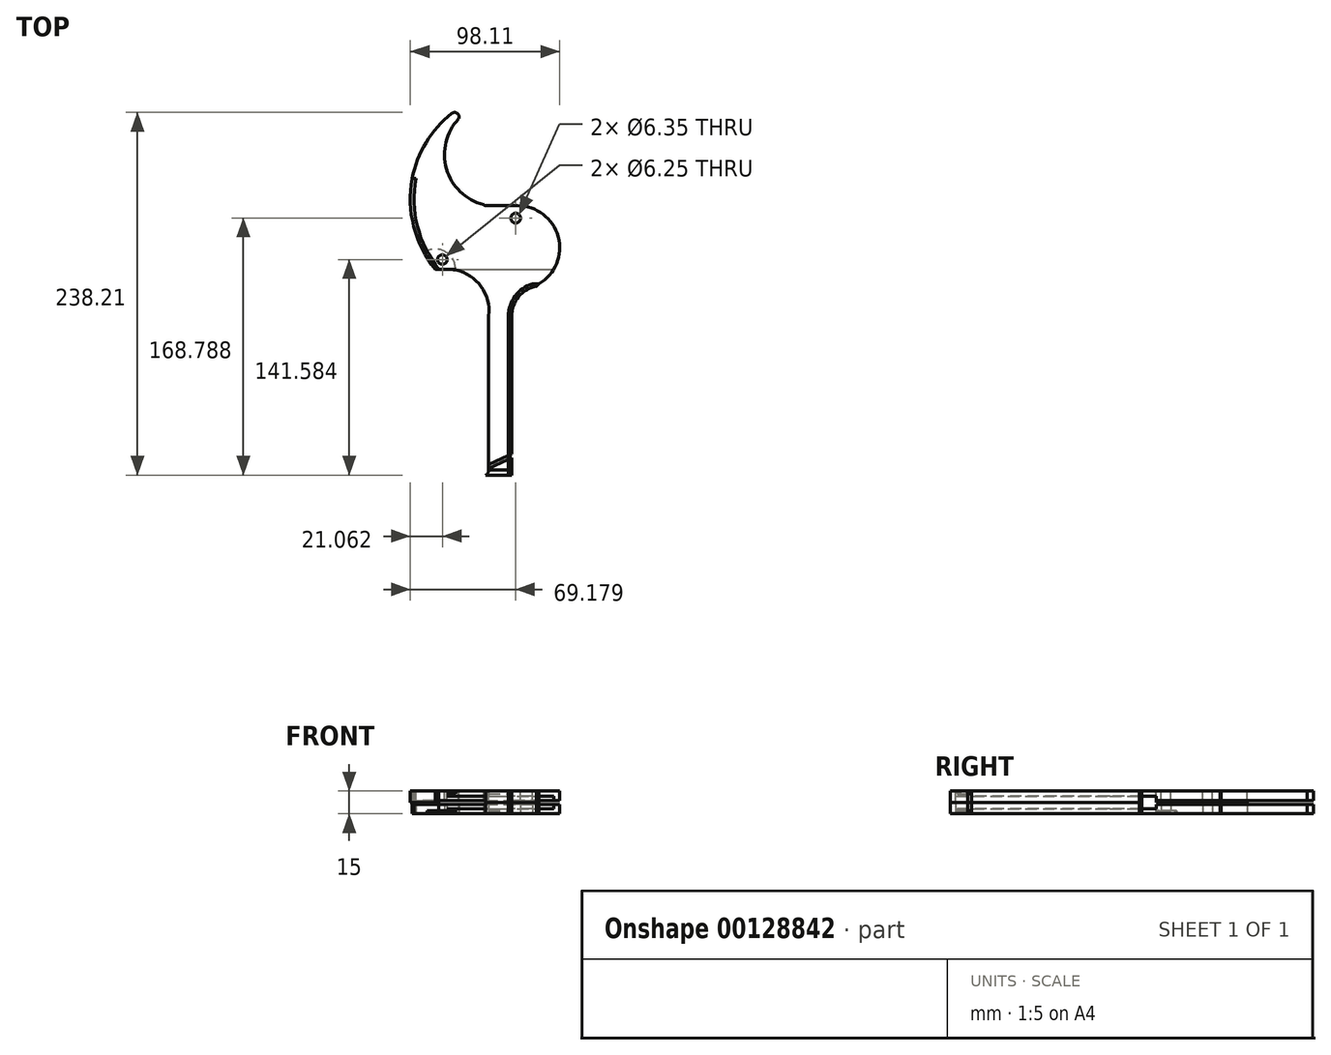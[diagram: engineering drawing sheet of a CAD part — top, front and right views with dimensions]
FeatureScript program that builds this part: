
annotation { "Feature Type Name" : "Feature", "Feature Type Description" : "" }
export const myFeature = defineFeature(function(context is Context, id is Id, definition is map)
    precondition{}
    {
        {
            var Q0;
            Q0=qCreatedBy(makeId("Top.planeOp"),FACE);
            var sketch = newSketch(context, id + "F0", { "sketchPlane" : qUnion([Q0])});
            skLineSegment(sketch, "E0", {"start": v(8.8, -17.92) * mm, "end": v(8.8, -59.13) * mm});
            skArc(sketch, "E1", {"start": v(-6.16, -17.65) * mm, "mid": v(-12.98, 3.75) * mm, "end": v(-33.49, 12.92) * mm});
            skLineSegment(sketch, "E2", {"start": v(-6.2, -18.21) * mm, "end": v(-6.2, -119.09) * mm});
            skArc(sketch, "E3", {"start": v(-8.08, -122.34) * mm, "mid": v(-6.7, -120.97) * mm, "end": v(-6.2, -119.09) * mm});
            skLineSegment(sketch, "E4", {"start": v(-8.08, -122.34) * mm, "end": v(8.8, -122.34) * mm});
            skLineSegment(sketch, "E5", {"start": v(8.8, -122.34) * mm, "end": v(8.8, -59.13) * mm});
            skArc(sketch, "E6.filletArc", {"start": v(8.92, 57.68) * mm, "mid": v(8.9, 57.68) * mm, "end": v(8.86, 57.67) * mm});
            skCircle(sketch, "E7", {"center": v(11.5, 46.45) * mm, "radius": 3.17 * mm});
            skCircle(sketch, "E8", {"center": v(-36.6, 19.24) * mm, "radius": 3.12 * mm});
            skPoint(sketch, "E9.visualSharp", {"position": v(8.8, -0.92) * mm});
            skArc(sketch, "E9.filletArc", {"start": v(25.2, 1.75) * mm, "mid": v(13.44, -5.12) * mm, "end": v(8.8, -17.92) * mm});
            skPoint(sketch, "E10.visualSharp", {"position": v(-6.2, -17.92) * mm});
            skArc(sketch, "E10.filletArc", {"start": v(-6.16, -17.65) * mm, "mid": v(-6.18, -17.93) * mm, "end": v(-6.2, -18.21) * mm});
            skLineSegment(sketch, "E11", {"start": v(-41.18, 12.92) * mm, "end": v(-33.49, 12.92) * mm});
            skLineSegment(sketch, "E12", {"start": v(-41.18, 12.92) * mm, "end": v(36.55, 12.92) * mm});
            skLineSegment(sketch, "E13.0", {"start": v(6.75, -122.34) * mm, "end": v(6.75, -59.13) * mm});
            skLineSegment(sketch, "E13.1", {"start": v(6.75, -17.92) * mm, "end": v(6.75, -59.13) * mm});
            skArc(sketch, "E13.2", {"start": v(22.5, 3.22) * mm, "mid": v(11.12, -4.74) * mm, "end": v(6.75, -17.92) * mm});
            skLineSegment(sketch, "E14", {"start": v(22.5, 3.22) * mm, "end": v(26.77, 3.22) * mm});
            skLineSegment(sketch, "E15", {"start": v(-40.58, 65.88) * mm, "end": v(-42.18, 65.88) * mm});
            skLineSegment(sketch, "E16", {"start": v(-6.2, -119.09) * mm, "end": v(6.75, -119.09) * mm});
            skArc(sketch, "E17", {"start": v(-30.51, 115.22) * mm, "mid": v(-57.28, 66.3) * mm, "end": v(-41.18, 12.92) * mm});
            skLineSegment(sketch, "E18", {"start": v(-7.81, 54.63) * mm, "end": v(12.85, 54.63) * mm});
            skArc(sketch, "E19", {"start": v(26.77, 3.22) * mm, "mid": v(39.48, 34.25) * mm, "end": v(12.85, 54.63) * mm});
            skPoint(sketch, "E20.visualSharp", {"position": v(-23.74, 120) * mm});
            skArc(sketch, "E20.filletArc", {"start": v(-25.85, 111.78) * mm, "mid": v(-26.86, 115.28) * mm, "end": v(-30.51, 115.22) * mm});
            skPoint(sketch, "E21.visualSharp", {"position": v(-8.79, 54.63) * mm});
            skArc(sketch, "E21.filletArc", {"start": v(-9.6, 55.22) * mm, "mid": v(-8.76, 54.78) * mm, "end": v(-7.81, 54.63) * mm});
            skLineSegment(sketch, "E22", {"start": v(-56.38, 72.41) * mm, "end": v(-53.97, 72.41) * mm});
            skArc(sketch, "E23", {"start": v(-53.97, 72.41) * mm, "mid": v(-52.92, 41.03) * mm, "end": v(-38.94, 12.92) * mm});
            skLineSegment(sketch, "E24", {"start": v(26.77, 3.22) * mm, "end": v(25.2, 1.75) * mm});
            skArc(sketch, "E25", {"start": v(-25.85, 111.78) * mm, "mid": v(-33.91, 78.85) * mm, "end": v(-9.6, 55.22) * mm});
            skSolve(sketch);
        }
        {
            var Q0;
            Q0=makeQuery(id+"F0.imprint","IMPRINT",FACE,{"disambiguationData":[TD([[makeQuery(id+"F0.imprint","IMPRINT",EDGE,{"derivedFrom":sQuery(id+"F0.wireOp",EDGE,"E0")}),-1.0]])]});
            extrude(context, id + "F1", {"entities" : qUnion([Q0]), "oppositeDirection" : true, "depth" : 7.5 * mm});
        }
        {
            var Q0;
            {var subQ0=sQuery(id+"F0.wireOp",EDGE,"E16");Q0=makeQuery(id+"F0.imprint","IMPRINT",FACE,{"disambiguationData":[TD([[makeQuery(id+"F0.imprint","IMPRINT",EDGE,{"derivedFrom":subQ0}),-1.0]])]});}
            extrude(context, id + "F2", {"entities" : qUnion([Q0]), "oppositeDirection" : true, "depth" : 7.5 * mm});
        }
        {
            var Q0;
            {var subQ1=sQuery(id+"F0.wireOp",EDGE,"E1");Q0=makeQuery(id+"F0.imprint","IMPRINT",FACE,{"disambiguationData":[TD([[makeQuery(id+"F0.imprint","IMPRINT",EDGE,{"derivedFrom":subQ1}),-1.0]])]});}
            extrude(context, id + "F3", {"entities" : qUnion([Q0]), "oppositeDirection" : true, "depth" : 3.33 * mm});
        }
        {
            var Q0;
            Q0=makeQuery(id+"F0.imprint","IMPRINT",FACE,{"disambiguationData":[TD([[makeQuery(id+"F0.imprint","IMPRINT",EDGE,{"derivedFrom":sQuery(id+"F0.wireOp",EDGE,"E7")}),-1.0]])]});
            extrude(context, id + "F4", {"entities" : qUnion([Q0]), "operationType" : NewBodyOperationType.ADD, "oppositeDirection" : true, "depth" : 6.14 * mm});
        }
        {
            var Q0;
            Q0=makeQuery(id+"F0.imprint","IMPRINT",FACE,{"disambiguationData":[TD([[makeQuery(id+"F0.imprint","IMPRINT",EDGE,{"derivedFrom":sQuery(id+"F0.wireOp",EDGE,"E0")}),-1.0]])]});
            var Q1;
            {var subQ4=sQuery(id+"F0.wireOp",EDGE,"E22");Q1=makeQuery(id+"F0.imprint","IMPRINT",FACE,{"disambiguationData":[TD([[makeQuery(id+"F0.imprint","IMPRINT",EDGE,{"derivedFrom":subQ4}),-1.0]])]});}
            extrude(context, id + "F5", {"entities" : qUnion([Q0, Q1]), "oppositeDirection" : true, "depth" : 7.5 * mm});
        }
        {
            var Q0;
            Q0=makeQuery(id+"F1.opExtrude","CAP_FACE",FACE,{"disambiguationData":[OSD([sQuery(id+"F0.wireOp",EDGE,"E0"),sQuery(id+"F0.wireOp",EDGE,"050fb45b-73f4-4136-bb6f-42e00f5a8c73"),sQuery(id+"F0.wireOp",EDGE,"E4"),sQuery(id+"F0.wireOp",EDGE,"E5"),sQuery(id+"F0.wireOp",EDGE,"E9.filletArc"),sQuery(id+"F0.wireOp",EDGE,"E13.0"),sQuery(id+"F0.wireOp",EDGE,"E13.1"),sQuery(id+"F0.wireOp",EDGE,"E13.2"),sQuery(id+"F0.wireOp",EDGE,"E14")])],"isStart":false});
            cPlane(context, id + "F6", {"entities" : qUnion([Q0]), "cplaneType" : CPlaneType.OFFSET, "offset" : 0 * mm, "width" : 150 * mm, "height" : 150 * mm});
        }
        {
            var Q0;
            Q0=makeQuery(id+"F3.opExtrude","CAP_FACE",FACE,{"disambiguationData":[OSD([sQuery(id+"F0.wireOp",EDGE,"050fb45b-73f4-4136-bb6f-42e00f5a8c73"),sQuery(id+"F0.wireOp",EDGE,"E1"),sQuery(id+"F0.wireOp",EDGE,"E2"),sQuery(id+"F0.wireOp",EDGE,"E10.filletArc"),sQuery(id+"F0.wireOp",EDGE,"E12"),sQuery(id+"F0.wireOp",EDGE,"E13.0"),sQuery(id+"F0.wireOp",EDGE,"E13.1"),sQuery(id+"F0.wireOp",EDGE,"E13.2"),sQuery(id+"F0.wireOp",EDGE,"E14"),sQuery(id+"F0.wireOp",EDGE,"E16")])],"isStart":true});
            var sketch = newSketch(context, id + "F7", { "sketchPlane" : qUnion([Q0])});
            skLineSegment(sketch, "E26", {"start": v(-6.2, -118.1) * mm, "end": v(8.8, -111.11) * mm});
            skLineSegment(sketch, "E27", {"start": v(-6.2, -115.32) * mm, "end": v(8.8, -108.33) * mm});
            skLineSegment(sketch, "E28", {"start": v(8.8, -108.33) * mm, "end": v(8.8, -111.11) * mm});
            skSolve(sketch);
        }
        {
            var Q0;
            {var subQ0=sQuery(id+"F7.wireOp",EDGE,"E26");var subQ1=makeQuery(id+"F3.opExtrude","CAP_EDGE",EDGE,{"disambiguationData":[OSD([sQuery(id+"F0.wireOp",EDGE,"E2")])],"isStart":true});var subQ2=makeQuery(id+"F7.imprint","INTERSECT",VERTEX,{"derivedFrom":[subQ1,subQ0]});Q0=makeQuery(id+"F7.imprint","IMPRINT",FACE,{"disambiguationData":[TD([[makeQuery(id+"F7.imprint","IMPRINT",EDGE,{"disambiguationData":[TD([[subQ2,1.0]])],"derivedFrom":subQ1}),1.0]])]});}
            var Q1;
            {var subQ0=sQuery(id+"F7.wireOp",EDGE,"E28");Q1=makeQuery(id+"F7.imprint","IMPRINT",FACE,{"disambiguationData":[TD([[makeQuery(id+"F7.imprint","IMPRINT",EDGE,{"derivedFrom":subQ0}),-1.0]])]});}
            extrude(context, id + "F8", {"entities" : qUnion([Q0, Q1]), "operationType" : NewBodyOperationType.REMOVE, "oppositeDirection" : true, "depth" : 2 * mm});
        }
        {
            var Q0;
            Q0=makeQuery(id+"F1.opExtrude","SWEPT_FACE",FACE,{"disambiguationData":[OSD([sQuery(id+"F0.wireOp",EDGE,"E0"),sQuery(id+"F0.wireOp",EDGE,"E5")])]});
            var sketch = newSketch(context, id + "F9", { "sketchPlane" : qUnion([Q0])});
            skLineSegment(sketch, "E29", {"start": v(-108.33, -2) * mm, "end": v(-108.33, -7.5) * mm});
            skLineSegment(sketch, "E30", {"start": v(-108.33, -7.5) * mm, "end": v(-111.11, -7.5) * mm});
            skLineSegment(sketch, "E31", {"start": v(-111.11, -7.5) * mm, "end": v(-111.11, -2) * mm});
            skSolve(sketch);
        }
        {
            var Q0;
            Q0=makeQuery(id+"F9.imprint","IMPRINT",FACE,{"disambiguationData":[TD([[makeQuery(id+"F9.imprint","IMPRINT",EDGE,{"derivedFrom":sQuery(id+"F9.wireOp",EDGE,"E29")}),-1.0]])]});
            extrude(context, id + "F10", {"entities" : qUnion([Q0]), "operationType" : NewBodyOperationType.REMOVE, "oppositeDirection" : true, "depth" : 2 * mm});
        }
        {
            var Q0;
            Q0=makeQuery(id+"F4.opExtrude","SWEPT_BODY",BODY,{"disambiguationData":[OSD([sQuery(id+"F0.wireOp",EDGE,"050fb45b-73f4-4136-bb6f-42e00f5a8c73"),sQuery(id+"F0.wireOp",EDGE,"ac5d1dc9-6bc1-422d-a1b8-74f4fc9e541e"),sQuery(id+"F0.wireOp",EDGE,"776ea0da-81a9-475d-bd45-8c6827eb6d53"),sQuery(id+"F0.wireOp",EDGE,"E6.filletArc"),sQuery(id+"F0.wireOp",EDGE,"E7"),sQuery(id+"F0.wireOp",EDGE,"E8"),sQuery(id+"F0.wireOp",EDGE,"d705c2e2-27fe-4b7d-9b31-5e995adf2de0.filletArc"),sQuery(id+"F0.wireOp",EDGE,"E12"),sQuery(id+"F0.wireOp",EDGE,"8f82b9b1-41a1-4198-a57d-b9d4a2749375"),sQuery(id+"F0.wireOp",EDGE,"E15")])]});
            var Q1;
            Q1=makeQuery(id+"F3.opExtrude","SWEPT_BODY",BODY,{"disambiguationData":[OSD([sQuery(id+"F0.wireOp",EDGE,"050fb45b-73f4-4136-bb6f-42e00f5a8c73"),sQuery(id+"F0.wireOp",EDGE,"E1"),sQuery(id+"F0.wireOp",EDGE,"E2"),sQuery(id+"F0.wireOp",EDGE,"E3"),sQuery(id+"F0.wireOp",EDGE,"E4"),sQuery(id+"F0.wireOp",EDGE,"E10.filletArc"),sQuery(id+"F0.wireOp",EDGE,"E12"),sQuery(id+"F0.wireOp",EDGE,"E13.0"),sQuery(id+"F0.wireOp",EDGE,"E13.1"),sQuery(id+"F0.wireOp",EDGE,"E13.2"),sQuery(id+"F0.wireOp",EDGE,"E14")])]});
            var Q2;
            Q2=makeQuery(id+"F1.opExtrude","SWEPT_BODY",BODY,{"disambiguationData":[OSD([sQuery(id+"F0.wireOp",EDGE,"E0"),sQuery(id+"F0.wireOp",EDGE,"050fb45b-73f4-4136-bb6f-42e00f5a8c73"),sQuery(id+"F0.wireOp",EDGE,"E4"),sQuery(id+"F0.wireOp",EDGE,"E5"),sQuery(id+"F0.wireOp",EDGE,"E9.filletArc"),sQuery(id+"F0.wireOp",EDGE,"E13.0"),sQuery(id+"F0.wireOp",EDGE,"E13.1"),sQuery(id+"F0.wireOp",EDGE,"E13.2"),sQuery(id+"F0.wireOp",EDGE,"E14")])]});
            var Q3;
            Q3=makeQuery(id+"F5.opExtrude","SWEPT_BODY",BODY,{"disambiguationData":[OSD([sQuery(id+"F0.wireOp",EDGE,"776ea0da-81a9-475d-bd45-8c6827eb6d53"),sQuery(id+"F0.wireOp",EDGE,"E12"),sQuery(id+"F0.wireOp",EDGE,"8f82b9b1-41a1-4198-a57d-b9d4a2749375"),sQuery(id+"F0.wireOp",EDGE,"E15")])]});
            var Q4;
            Q4=makeQuery(id+"F2.opExtrude","SWEPT_BODY",BODY,{"disambiguationData":[OSD([sQuery(id+"F0.wireOp",EDGE,"E3"),sQuery(id+"F0.wireOp",EDGE,"E4"),sQuery(id+"F0.wireOp",EDGE,"E13.0"),sQuery(id+"F0.wireOp",EDGE,"E16")])]});
            var Q5;
            Q5=qCreatedBy(id+"F6.planeOp",FACE);
            mirror(context, id + "F11", {"entities" : qUnion([Q0, Q1, Q2, Q3, Q4]), "mirrorPlane" : qUnion([Q5])});
        }
        {
            var Q0;
            Q0=makeQuery(id+"F0.imprint","IMPRINT",FACE,{"disambiguationData":[TD([[makeQuery(id+"F0.imprint","IMPRINT",EDGE,{"derivedFrom":sQuery(id+"F0.wireOp",EDGE,"E7")}),-1.0]])]});
            cPlane(context, id + "F12", {"entities" : qUnion([Q0]), "cplaneType" : CPlaneType.OFFSET, "offset" : 0 * mm, "width" : 150 * mm, "height" : 150 * mm});
        }
        {
            var Q0;
            Q0=qCreatedBy(id+"F12.planeOp",FACE);
            var sketch = newSketch(context, id + "F13", { "sketchPlane" : qUnion([Q0])});
            skLineSegment(sketch, "E32.0", {"start": v(-38.94, 12.92) * mm, "end": v(-38.94, 12.92) * mm});
            skArc(sketch, "E33.0", {"start": v(-6.16, -17.65) * mm, "mid": v(-12.98, 3.75) * mm, "end": v(-33.49, 12.92) * mm});
            skLineSegment(sketch, "E34", {"start": v(-27.96, 12.92) * mm, "end": v(-27.96, 12.36) * mm});
            skArc(sketch, "E35.0", {"start": v(-30.51, 115.22) * mm, "mid": v(-57.28, 66.3) * mm, "end": v(-41.18, 12.92) * mm});
            skArc(sketch, "E36", {"start": v(-48.62, 23.84) * mm, "mid": v(-35, 24.6) * mm, "end": v(-27.96, 12.92) * mm});
            skLineSegment(sketch, "E37", {"start": v(-27.96, 12.92) * mm, "end": v(-41.18, 12.92) * mm});
            skSolve(sketch);
        }
        {
            var Q0;
            {var subQ3=sQuery(id+"F13.wireOp",EDGE,"E36");Q0=makeQuery(id+"F13.imprint","IMPRINT",FACE,{"disambiguationData":[TD([[makeQuery(id+"F13.imprint","IMPRINT",EDGE,{"derivedFrom":subQ3}),-1.0]])]});}
            var Q1;
            {var subQ3=sQuery(id+"F13.wireOp",EDGE,"E34");Q1=makeQuery(id+"F13.imprint","IMPRINT",FACE,{"disambiguationData":[TD([[makeQuery(id+"F13.imprint","IMPRINT",EDGE,{"derivedFrom":subQ3}),-1.0]])]});}
            extrude(context, id + "F14", {"entities" : qUnion([Q0, Q1]), "operationType" : NewBodyOperationType.REMOVE, "oppositeDirection" : true, "depth" : 2 * mm});
        }
        {
            var Q0;
            {var subQ0=sQuery(id+"F0.wireOp",EDGE,"E7");var subQ1=sQuery(id+"F0.wireOp",EDGE,"E19");var subQ2=sQuery(id+"F0.wireOp",EDGE,"E14");var subQ3=sQuery(id+"F0.wireOp",EDGE,"E13.2");var subQ4=sQuery(id+"F0.wireOp",EDGE,"E1");var subQ5=sQuery(id+"F0.wireOp",EDGE,"E8");var subQ6=sQuery(id+"F0.wireOp",EDGE,"E2");var subQ7=sQuery(id+"F0.wireOp",EDGE,"E12");var subQ8=sQuery(id+"F0.wireOp",EDGE,"E10.filletArc");var subQ9=sQuery(id+"F0.wireOp",EDGE,"E18");var subQ10=sQuery(id+"F0.wireOp",EDGE,"E13.1");var subQ11=sQuery(id+"F0.wireOp",EDGE,"E13.0");var subQ12=sQuery(id+"F0.wireOp",EDGE,"E21.filletArc");var subQ13=sQuery(id+"F0.wireOp",EDGE,"E17");var subQ14=sQuery(id+"F0.wireOp",EDGE,"E20.filletArc");var subQ15=sQuery(id+"F0.wireOp",EDGE,"E22");var subQ16=sQuery(id+"F0.wireOp",EDGE,"E23");var subQ17=sQuery(id+"F0.wireOp",EDGE,"E25");Q0=makeQuery(id+"F11.opPattern","COPY",FACE,{"derivedFrom":makeQuery(id+"F8.boolean.opBoolean","SPLIT",FACE,{"disambiguationData":[TD([makeQuery(id+"F3.opExtrude","SWEPT_FACE",FACE,{"disambiguationData":[OSD([subQ4])]})])],"derivedFrom":makeQuery(id+"F4.boolean.opBoolean","MERGE",FACE,{"derivedFrom":[makeQuery(id+"F3.opExtrude","CAP_FACE",FACE,{"disambiguationData":[OSD([subQ4,subQ6,subQ8,subQ7,subQ11,subQ10,subQ3,subQ2,sQuery(id+"F0.wireOp",EDGE,"E16"),subQ1])],"isStart":true}),makeQuery(id+"F4.opExtrude","CAP_FACE",FACE,{"disambiguationData":[OSD([subQ0,subQ5,subQ7,subQ13,subQ9,subQ1,subQ14,subQ12,subQ15,subQ16,subQ17])],"isStart":true})]})}),"instanceName":"1"});}
            cPlane(context, id + "F15", {"entities" : qUnion([Q0]), "cplaneType" : CPlaneType.OFFSET, "offset" : 0 * mm, "width" : 150 * mm, "height" : 150 * mm});
        }
        {
            var Q0;
            Q0=qCreatedBy(id+"F15.planeOp",FACE);
            var sketch = newSketch(context, id + "F16", { "sketchPlane" : qUnion([Q0])});
            skArc(sketch, "E38.0", {"start": v(-30.51, -115.22) * mm, "mid": v(-57.28, -66.3) * mm, "end": v(-41.18, -12.92) * mm});
            skArc(sketch, "E39", {"start": v(-48.62, -23.84) * mm, "mid": v(-35, -24.6) * mm, "end": v(-27.96, -12.92) * mm});
            skArc(sketch, "E40.0", {"start": v(-6.16, 17.65) * mm, "mid": v(-12.98, -3.75) * mm, "end": v(-33.49, -12.92) * mm});
            skLineSegment(sketch, "E41", {"start": v(-27.96, -12.92) * mm, "end": v(-27.96, -12.36) * mm});
            skLineSegment(sketch, "E42", {"start": v(-33.49, -12.92) * mm, "end": v(-41.18, -12.92) * mm});
            skSolve(sketch);
        }
        {
            var Q0;
            {var subQ3=sQuery(id+"F16.wireOp",EDGE,"E39");Q0=makeQuery(id+"F16.imprint","IMPRINT",FACE,{"disambiguationData":[TD([[makeQuery(id+"F16.imprint","IMPRINT",EDGE,{"derivedFrom":subQ3}),1.0]])]});}
            extrude(context, id + "F17", {"entities" : qUnion([Q0]), "operationType" : NewBodyOperationType.REMOVE, "oppositeDirection" : true, "depth" : 2 * mm});
        }
    });
